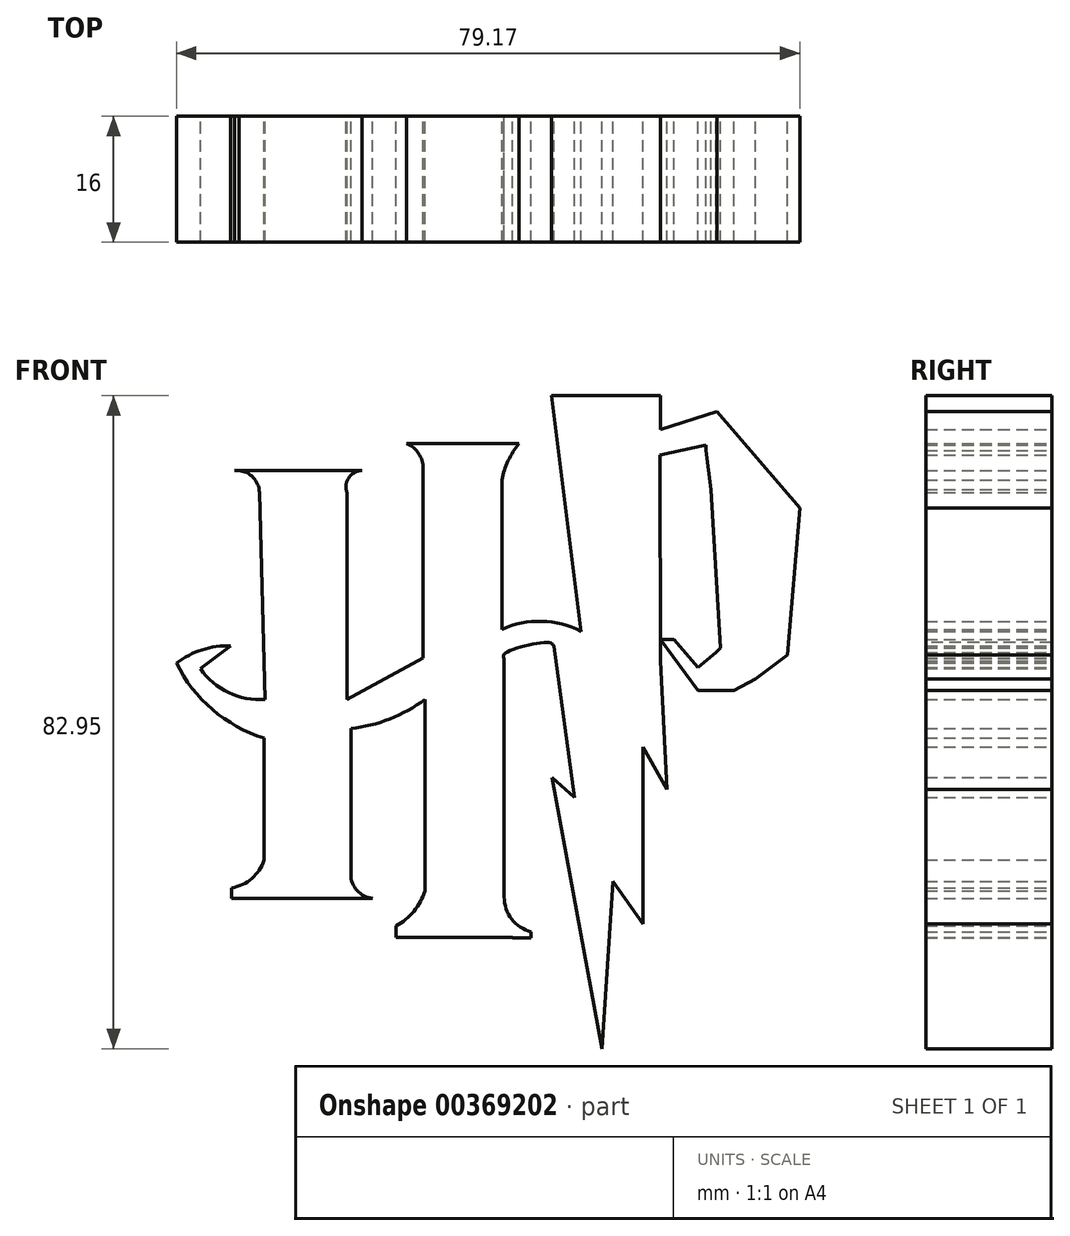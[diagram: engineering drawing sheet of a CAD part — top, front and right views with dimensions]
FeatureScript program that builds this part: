
annotation { "Feature Type Name" : "Feature", "Feature Type Description" : "" }
export const myFeature = defineFeature(function(context is Context, id is Id, definition is map)
    precondition{}
    {
        {
            var Q0;
            Q0=qCreatedBy(makeId("Front.planeOp"),FACE);
            var sketch = newSketch(context, id + "F0", { "sketchPlane" : qUnion([Q0])});
            skLineSegment(sketch, "E0", {"start": v(13.24, 38.57) * mm, "end": v(16.98, 8.63) * mm});
            skLineSegment(sketch, "E1", {"start": v(13.24, 38.57) * mm, "end": v(27.05, 38.57) * mm});
            skLineSegment(sketch, "E2", {"start": v(27.05, 34.25) * mm, "end": v(27.05, 38.57) * mm});
            skLineSegment(sketch, "E3", {"start": v(27.05, 34.25) * mm, "end": v(34.25, 36.55) * mm});
            skLineSegment(sketch, "E4", {"start": v(34.25, 36.55) * mm, "end": v(44.75, 24.32) * mm});
            skLineSegment(sketch, "E5", {"start": v(44.75, 24.32) * mm, "end": v(43.17, 5.61) * mm});
            skLineSegment(sketch, "E6", {"start": v(43.17, 5.61) * mm, "end": v(39.14, 2.6) * mm});
            skLineSegment(sketch, "E7", {"start": v(39.14, 2.6) * mm, "end": v(36.4, 1.15) * mm});
            skLineSegment(sketch, "E8", {"start": v(36.4, 1.15) * mm, "end": v(31.8, 1.15) * mm});
            skLineSegment(sketch, "E9", {"start": v(31.8, 1.15) * mm, "end": v(27.05, 7.63) * mm});
            skLineSegment(sketch, "E10", {"start": v(27.05, 7.63) * mm, "end": v(28.78, 7.63) * mm});
            skLineSegment(sketch, "E11", {"start": v(28.78, 7.63) * mm, "end": v(31.8, 4.03) * mm});
            skLineSegment(sketch, "E12", {"start": v(31.8, 4.03) * mm, "end": v(34.1, 5.96) * mm});
            skLineSegment(sketch, "E13", {"start": v(34.1, 5.96) * mm, "end": v(34.68, 6.55) * mm});
            skLineSegment(sketch, "E14", {"start": v(34.68, 6.55) * mm, "end": v(33.46, 26.62) * mm});
            skLineSegment(sketch, "E15", {"start": v(33.46, 26.62) * mm, "end": v(32.8, 31.59) * mm});
            skLineSegment(sketch, "E16", {"start": v(32.8, 31.59) * mm, "end": v(32.8, 32.3) * mm});
            skLineSegment(sketch, "E17", {"start": v(32.8, 32.3) * mm, "end": v(26.98, 31.01) * mm});
            skLineSegment(sketch, "E18", {"start": v(26.98, 31.01) * mm, "end": v(27.05, 4.9) * mm});
            skLineSegment(sketch, "E19", {"start": v(27.05, 4.9) * mm, "end": v(27.86, -11.44) * mm});
            skLineSegment(sketch, "E20", {"start": v(27.86, -11.44) * mm, "end": v(24.86, -6.05) * mm});
            skLineSegment(sketch, "E21", {"start": v(24.86, -6.05) * mm, "end": v(24.86, -28.55) * mm});
            skLineSegment(sketch, "E22", {"start": v(24.86, -28.55) * mm, "end": v(21, -23.16) * mm});
            skLineSegment(sketch, "E23", {"start": v(21, -23.16) * mm, "end": v(19.63, -44.38) * mm});
            skLineSegment(sketch, "E24", {"start": v(19.63, -44.38) * mm, "end": v(13.3, -9.9) * mm});
            skLineSegment(sketch, "E25", {"start": v(13.3, -9.9) * mm, "end": v(16.12, -12.46) * mm});
            skLineSegment(sketch, "E26", {"start": v(16.12, -12.46) * mm, "end": v(13.52, 6.7) * mm});
            skFitSpline(sketch, "E27", {"points": [v(13.52, 6.7) * mm, v(12.89, 7.2) * mm, v(7.2, 5.75) * mm, v(7.2, 5.2) * mm], "startDerivative": vector(-1.24, 2.94) * mm, "endDerivative": vector(1.62, -2.84) * mm});
            skLineSegment(sketch, "E28", {"start": v(7.2, 5.2) * mm, "end": v(7.2, -25.11) * mm});
            skArc(sketch, "E29", {"start": v(7.2, -25.11) * mm, "mid": v(8.16, -27.92) * mm, "end": v(10.63, -29.56) * mm});
            skLineSegment(sketch, "E30", {"start": v(10.63, -29.56) * mm, "end": v(10.63, -30.3) * mm});
            skLineSegment(sketch, "E31", {"start": v(10.63, -30.3) * mm, "end": v(8.26, -30.3) * mm});
            skLineSegment(sketch, "E32", {"start": v(8.26, -30.3) * mm, "end": v(8.26, -30.26) * mm});
            skLineSegment(sketch, "E33", {"start": v(8.26, -30.26) * mm, "end": v(-6.54, -30.26) * mm});
            skLineSegment(sketch, "E34", {"start": v(-6.54, -30.26) * mm, "end": v(-6.54, -28.8) * mm});
            skArc(sketch, "E35", {"start": v(-6.54, -28.8) * mm, "mid": v(-4.27, -26.91) * mm, "end": v(-2.86, -24.31) * mm});
            skLineSegment(sketch, "E36", {"start": v(-2.86, -24.31) * mm, "end": v(-2.86, 0) * mm});
            skArc(sketch, "E37", {"start": v(-12.28, -3.72) * mm, "mid": v(-7.32, -2.49) * mm, "end": v(-2.86, 0) * mm});
            skLineSegment(sketch, "E38", {"start": v(-12.28, -3.72) * mm, "end": v(-12.28, -22.24) * mm});
            skArc(sketch, "E39", {"start": v(-12.28, -22.24) * mm, "mid": v(-11.48, -24.3) * mm, "end": v(-9.5, -25.26) * mm});
            skLineSegment(sketch, "E40", {"start": v(-9.5, -25.26) * mm, "end": v(-27.4, -25.26) * mm});
            skArc(sketch, "E41", {"start": v(-27.4, -23.93) * mm, "mid": v(-24.85, -22.76) * mm, "end": v(-23.29, -20.42) * mm});
            skLineSegment(sketch, "E42", {"start": v(-27.4, -23.93) * mm, "end": v(-27.4, -25.26) * mm});
            skLineSegment(sketch, "E43", {"start": v(-23.29, -20.42) * mm, "end": v(-23.29, -4.94) * mm});
            skArc(sketch, "E44", {"start": v(-34.42, 4.62) * mm, "mid": v(-29.85, -1.31) * mm, "end": v(-23.29, -4.94) * mm});
            skArc(sketch, "E45", {"start": v(-27.52, 6.8) * mm, "mid": v(-31.16, 6.3) * mm, "end": v(-34.42, 4.62) * mm});
            skLineSegment(sketch, "E46", {"start": v(-27.52, 6.8) * mm, "end": v(-31.4, 3.9) * mm});
            skArc(sketch, "E47", {"start": v(-31.4, 3.9) * mm, "mid": v(-27.8, 0.85) * mm, "end": v(-23.17, 0) * mm});
            skLineSegment(sketch, "E48", {"start": v(-23.17, 0) * mm, "end": v(-23.9, 26.28) * mm});
            skArc(sketch, "E49", {"start": v(-23.9, 26.28) * mm, "mid": v(-24.86, 28.36) * mm, "end": v(-27.04, 29.07) * mm});
            skLineSegment(sketch, "E50", {"start": v(-27.04, 29.07) * mm, "end": v(-10.83, 29.07) * mm});
            skArc(sketch, "E51", {"start": v(-10.83, 29.07) * mm, "mid": v(-12.52, 28.18) * mm, "end": v(-12.76, 26.28) * mm});
            skLineSegment(sketch, "E52", {"start": v(-12.76, 26.28) * mm, "end": v(-12.76, 0) * mm});
            skLineSegment(sketch, "E53", {"start": v(-12.76, 0) * mm, "end": v(-3.08, 5.23) * mm});
            skLineSegment(sketch, "E54", {"start": v(-3.08, 5.23) * mm, "end": v(-3.08, 29.31) * mm});
            skArc(sketch, "E55", {"start": v(-3.08, 29.31) * mm, "mid": v(-3.65, 31.22) * mm, "end": v(-5.18, 32.5) * mm});
            skLineSegment(sketch, "E56", {"start": v(-5.18, 32.5) * mm, "end": v(9.1, 32.5) * mm});
            skArc(sketch, "E57", {"start": v(9.1, 32.5) * mm, "mid": v(7.7, 30.31) * mm, "end": v(6.91, 27.84) * mm});
            skLineSegment(sketch, "E58", {"start": v(6.91, 27.84) * mm, "end": v(6.91, 8.88) * mm});
            skArc(sketch, "E59", {"start": v(16.98, 8.63) * mm, "mid": v(11.98, 9.9) * mm, "end": v(6.91, 8.88) * mm});
            skSolve(sketch);
        }
        {
            var Q0;
            Q0 = qSketchRegion(id + "F0", true);
            extrude(context, id + "F1", {"entities" : qUnion([Q0]), "depth" : 16 * mm});
        }
    });
